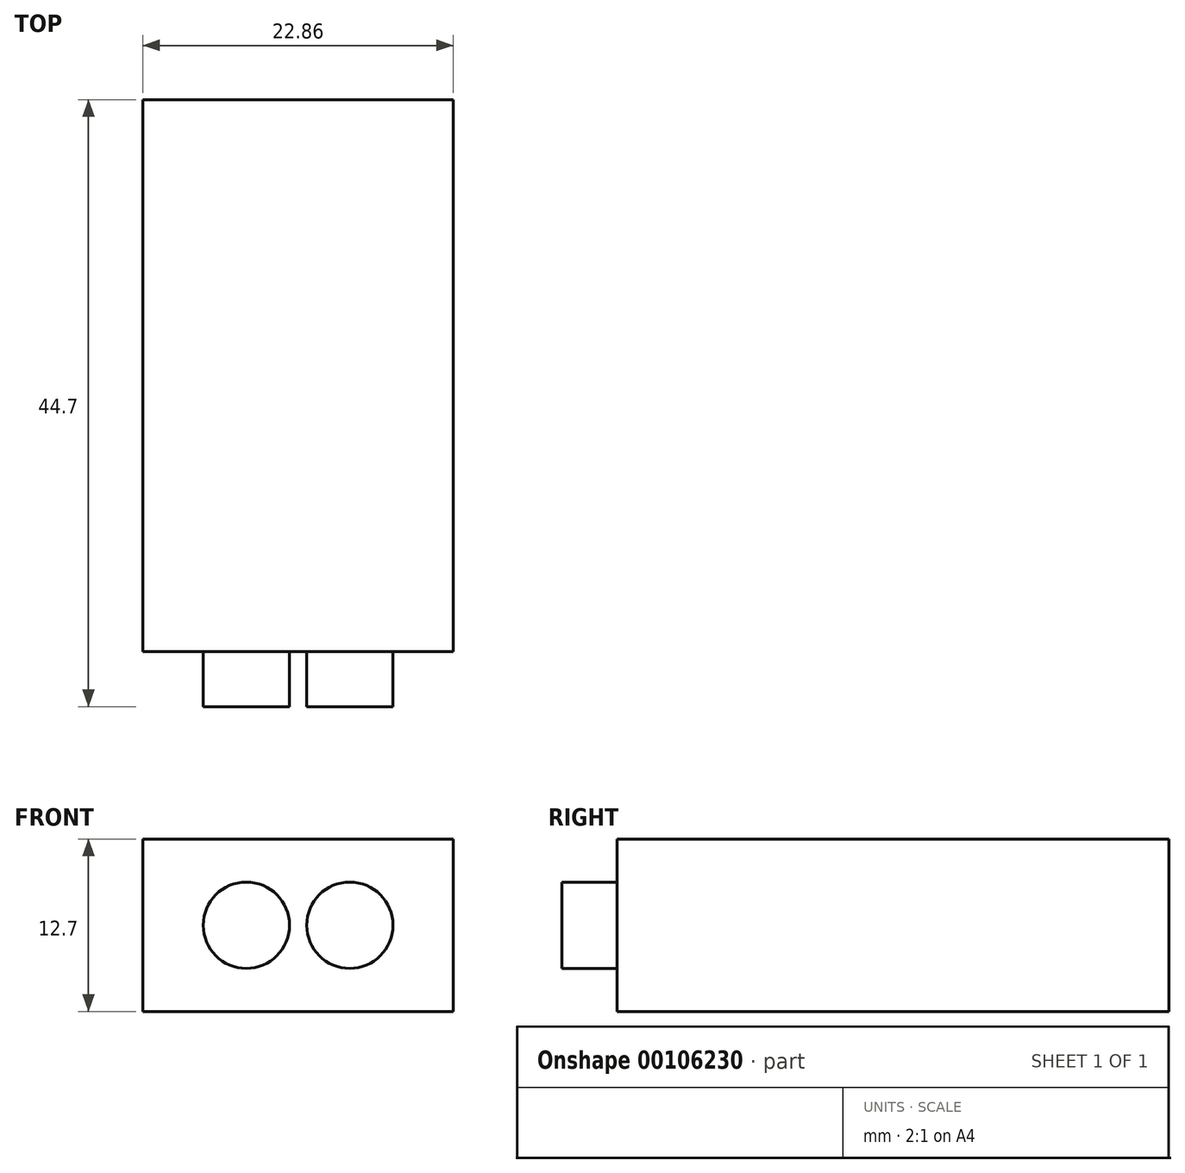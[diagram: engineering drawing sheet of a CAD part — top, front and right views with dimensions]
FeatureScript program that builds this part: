
annotation { "Feature Type Name" : "Feature", "Feature Type Description" : "" }
export const myFeature = defineFeature(function(context is Context, id is Id, definition is map)
    precondition{}
    {
        {
            var Q0;
            Q0=qCreatedBy(makeId("Top.planeOp"),FACE);
            var sketch = newSketch(context, id + "F0", { "sketchPlane" : qUnion([Q0])});
            skLineSegment(sketch, "E0", {"start": v(-25, 28.14) * mm, "end": v(-2.14, 28.14) * mm});
            skLineSegment(sketch, "E1", {"start": v(-25, 28.14) * mm, "end": v(-25, -12.5) * mm});
            skLineSegment(sketch, "E2", {"start": v(-25, -12.5) * mm, "end": v(-2.14, -12.5) * mm});
            skLineSegment(sketch, "E3", {"start": v(-2.14, -12.5) * mm, "end": v(-2.14, 28.14) * mm});
            skSolve(sketch);
        }
        {
            var Q0;
            Q0 = qSketchRegion(id + "F0", true);
            extrude(context, id + "F1", {"entities" : qUnion([Q0]), "depth" : 12.7 * mm});
        }
        {
            var Q0;
            Q0=makeQuery(id+"F1.opExtrude","SWEPT_FACE",FACE,{"disambiguationData":[OSD([sQuery(id+"F0.wireOp",EDGE,"E2")])]});
            var sketch = newSketch(context, id + "F2", { "sketchPlane" : qUnion([Q0])});
            skCircle(sketch, "E4", {"center": v(-17.38, 6.35) * mm, "radius": 3.18 * mm});
            skCircle(sketch, "E5", {"center": v(-9.76, 6.35) * mm, "radius": 3.18 * mm});
            skSolve(sketch);
        }
        {
            var Q0;
            Q0 = qSketchRegion(id + "F2", true);
            extrude(context, id + "F3", {"entities" : qUnion([Q0]), "operationType" : NewBodyOperationType.ADD, "depth" : 4.06 * mm});
        }
    });
